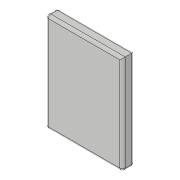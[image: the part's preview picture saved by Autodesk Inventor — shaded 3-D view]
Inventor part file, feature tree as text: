
AUTODESK INVENTOR PART (.ipt)
format: ipt  version: 2018.3 (Build 223284000, 284)  size: 93,696 bytes
history: native  units: in
note: dims shown in document units (in); Inventor stores cm internally (conversion verified against a paired STEP export)
features: extrude x1, fillet x1, sketch x1
ambient origin geometry x8: Origin, YZ Plane, XZ Plane, XY Plane, X Axis, Y Axis, Z Axis, Center Point
bodies: Solid1 (feature_tree)
feature tree (3):
  extrude  "Extrusion1"  Depth=2.35in
  fillet  "Fillet1"  Radius=0.28in
  sketch  "Sketch1"  dims[d0=1.825in d1=2.35in d2=0.28in d3=0.0in d4=0.0625in]
